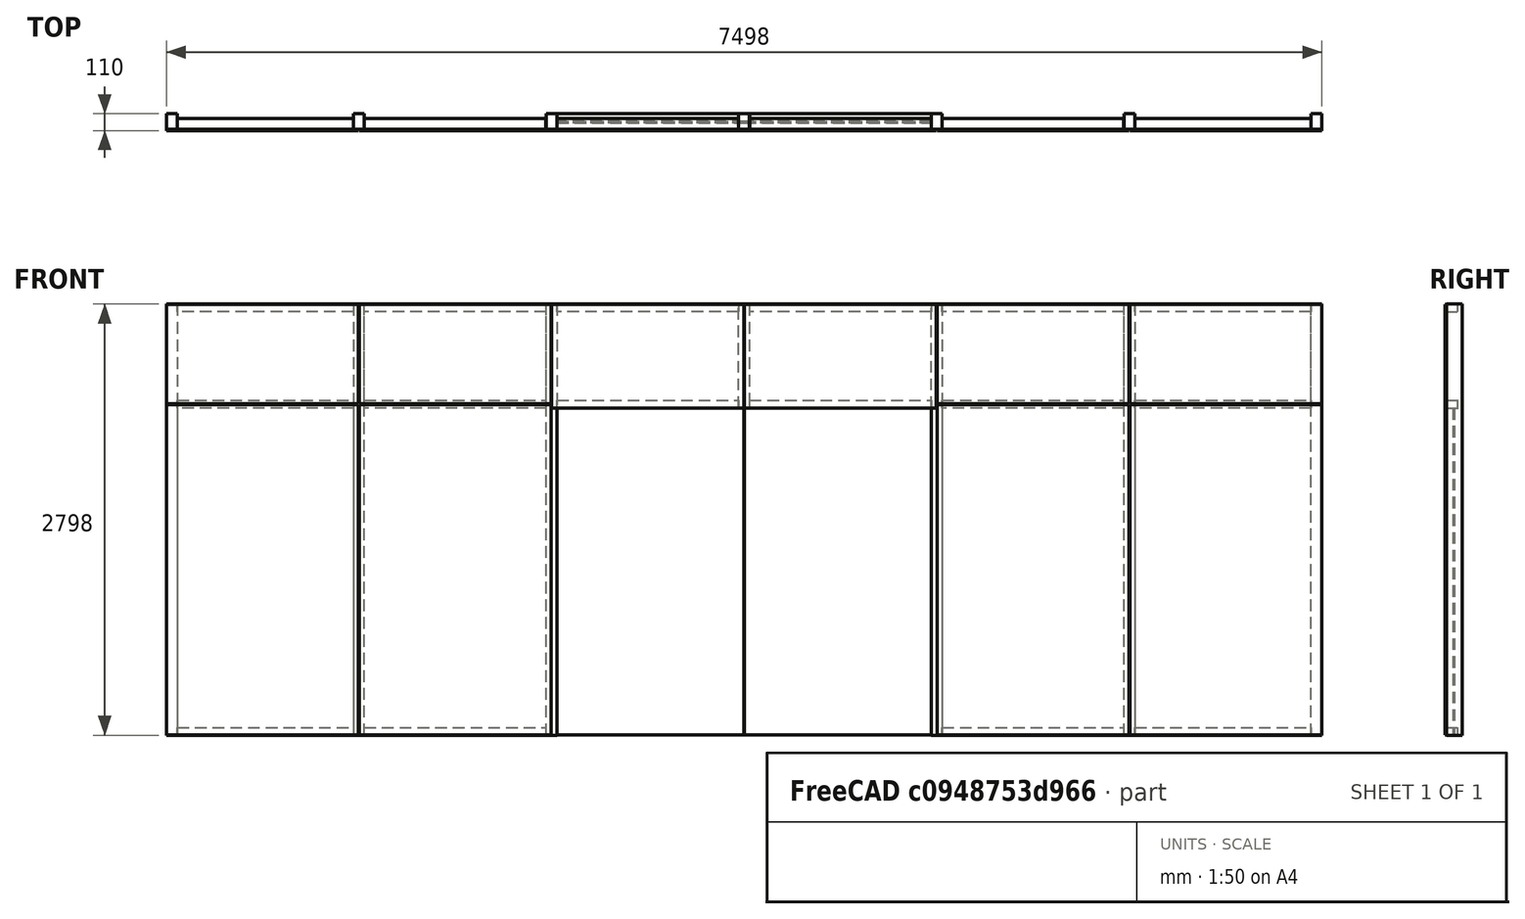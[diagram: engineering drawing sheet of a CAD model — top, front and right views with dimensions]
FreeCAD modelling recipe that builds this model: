
FCSTD DOCUMENT  (FreeCAD 0.16R6704 (Git))
Label: glass skin 6 modules and doors
License: CreativeCommons Attribution
LicenseURL: http://creativecommons.org/licenses/by/4.0/
objects: Sketcher::SketchObject×1, Part::FeaturePython×1
note: 2 computed .brp shape members not serialized (recipe doc carries the construction recipe); baked Part::Feature solids carry a one-line shape summary decoded from their .brp

FEATURE [Sketcher::SketchObject] Sketch207  label="Esboço pele de vidro 002"
  Placement = pos=(0,0,0) rot=(1,0,0;1.5708rad)
  sketch-geometry (176):
    g0: LineSegment StartX=0 StartY=0 StartZ=0 EndX=7500 EndY=0 EndZ=0
    g1: LineSegment StartX=7500 StartY=0 StartZ=0 EndX=7500 EndY=2800 EndZ=0
    g2: LineSegment StartX=7500 StartY=2800 StartZ=0 EndX=0 EndY=2800 EndZ=0
    g3: LineSegment StartX=0 StartY=2800 StartZ=0 EndX=0 EndY=0 EndZ=0
    g4: LineSegment StartX=1 StartY=2799 StartZ=0 EndX=71 EndY=2799 EndZ=0
    g5: LineSegment StartX=71 StartY=2799 StartZ=0 EndX=71 EndY=1 EndZ=0
    g6: LineSegment StartX=71 StartY=1 StartZ=0 EndX=1 EndY=1 EndZ=0
    g7: LineSegment StartX=1 StartY=1 StartZ=0 EndX=1 EndY=2799 EndZ=0
    g8: LineSegment StartX=1285 StartY=2799 StartZ=0 EndX=1215 EndY=2799 EndZ=0
    g9: LineSegment StartX=1215 StartY=2799 StartZ=0 EndX=1215 EndY=1 EndZ=0
    g10: LineSegment StartX=1215 StartY=1 StartZ=0 EndX=1285 EndY=1 EndZ=0
    g11: LineSegment StartX=1285 StartY=1 StartZ=0 EndX=1285 EndY=2799 EndZ=0
    g12: LineSegment StartX=72 StartY=2799 StartZ=0 EndX=1214 EndY=2799 EndZ=0
    g13: LineSegment StartX=1214 StartY=2799 StartZ=0 EndX=1214 EndY=2749 EndZ=0
    g14: LineSegment StartX=1214 StartY=2749 StartZ=0 EndX=72 EndY=2749 EndZ=0
    g15: LineSegment StartX=72 StartY=2749 StartZ=0 EndX=72 EndY=2799 EndZ=0
    g16: LineSegment StartX=72 StartY=2175 StartZ=0 EndX=1214 EndY=2175 EndZ=0
    g17: LineSegment StartX=1214 StartY=2175 StartZ=0 EndX=1214 EndY=2125 EndZ=0
    g18: LineSegment StartX=1214 StartY=2125 StartZ=0 EndX=72 EndY=2125 EndZ=0
    g19: LineSegment StartX=72 StartY=2125 StartZ=0 EndX=72 EndY=2175 EndZ=0
    g20: LineSegment StartX=72 StartY=51 StartZ=0 EndX=1214 EndY=51 EndZ=0
    g21: LineSegment StartX=1214 StartY=51 StartZ=0 EndX=1214 EndY=1 EndZ=0
    g22: LineSegment StartX=1214 StartY=1 StartZ=0 EndX=72 EndY=1 EndZ=0
    g23: LineSegment StartX=72 StartY=1 StartZ=0 EndX=72 EndY=51 EndZ=0
    g24: LineSegment [constr] StartX=0 StartY=4045.56 StartZ=0 EndX=0 EndY=0 EndZ=0
    g25: LineSegment [constr] StartX=1250 StartY=4032 StartZ=0 EndX=1250 EndY=-1064.23 EndZ=0
    g26: LineSegment [constr] StartX=2500 StartY=4059.26 StartZ=0 EndX=2500 EndY=-1119 EndZ=0
    g27: LineSegment [constr] StartX=3750 StartY=3908.57 StartZ=0 EndX=3750 EndY=-1023 EndZ=0
    g28: LineSegment [constr] StartX=5000 StartY=3990.77 StartZ=0 EndX=5000 EndY=-934.694 EndZ=0
    g29: LineSegment [constr] StartX=6250 StartY=4286.35 StartZ=0 EndX=6250 EndY=-1160 EndZ=0
    g30: LineSegment [constr] StartX=7500 StartY=4004.47 StartZ=0 EndX=7500 EndY=0 EndZ=0
    g31: LineSegment [constr] StartX=-2084.05 StartY=2150 StartZ=0 EndX=-4913.6 EndY=2150 EndZ=0
    g32: LineSegment [constr] StartX=0 StartY=3388 StartZ=0 EndX=1250 EndY=3388 EndZ=0
    g33: LineSegment [constr] StartX=1250 StartY=3579.79 StartZ=0 EndX=2500 EndY=3579.79 EndZ=0
    g34: LineSegment [constr] StartX=2500 StartY=3223.61 StartZ=0 EndX=3750 EndY=3223.61 EndZ=0
    g35: LineSegment [constr] StartX=3750 StartY=3538.69 StartZ=0 EndX=5000 EndY=3538.69 EndZ=0
    g36: LineSegment [constr] StartX=5000 StartY=3210 StartZ=0 EndX=6250 EndY=3210 EndZ=0
    g37: LineSegment [constr] StartX=6250 StartY=3579.79 StartZ=0 EndX=7500 EndY=3579.79 EndZ=0
    g38: LineSegment [constr] StartX=287.264 StartY=2799 StartZ=0 EndX=287.264 EndY=2749 EndZ=0
    g39: LineSegment [constr] StartX=206.222 StartY=2175 StartZ=0 EndX=206.222 EndY=2125 EndZ=0
    g40: LineSegment [constr] StartX=1 StartY=2367.03 StartZ=0 EndX=71 EndY=2367.03 EndZ=0
    g41: LineSegment [constr] StartX=1215 StartY=2396.22 StartZ=0 EndX=1285 EndY=2396.22 EndZ=0
    g42: LineSegment [constr] StartX=456.696 StartY=51 StartZ=0 EndX=456.696 EndY=1 EndZ=0
    g43: LineSegment StartX=2.5 StartY=2797.5 StartZ=0 EndX=1247.5 EndY=2797.5 EndZ=0
    g44: LineSegment StartX=1247.5 StartY=2797.5 StartZ=0 EndX=1247.5 EndY=2152.5 EndZ=0
    g45: LineSegment StartX=1247.5 StartY=2152.5 StartZ=0 EndX=2.5 EndY=2152.5 EndZ=0
    g46: LineSegment StartX=2.5 StartY=2152.5 StartZ=0 EndX=2.5 EndY=2797.5 EndZ=0
    g47: LineSegment StartX=2465 StartY=2799 StartZ=0 EndX=2535 EndY=2799 EndZ=0
    g48: LineSegment StartX=2535 StartY=2799 StartZ=0 EndX=2535 EndY=1 EndZ=0
    g49: LineSegment StartX=2535 StartY=1 StartZ=0 EndX=2465 EndY=1 EndZ=0
    g50: LineSegment StartX=2465 StartY=1 StartZ=0 EndX=2465 EndY=2799 EndZ=0
    g51: LineSegment StartX=3715 StartY=2799 StartZ=0 EndX=3785 EndY=2799 EndZ=0
    g52: LineSegment StartX=3785 StartY=2799 StartZ=0 EndX=3785 EndY=2125 EndZ=0
    g53: LineSegment StartX=3785 StartY=2125 StartZ=0 EndX=3715 EndY=2125 EndZ=0
    g54: LineSegment StartX=3715 StartY=2125 StartZ=0 EndX=3715 EndY=2799 EndZ=0
    g55: LineSegment StartX=4965 StartY=2799 StartZ=0 EndX=5035 EndY=2799 EndZ=0
    g56: LineSegment StartX=5035 StartY=2799 StartZ=0 EndX=5035 EndY=1 EndZ=0
    g57: LineSegment StartX=5035 StartY=1 StartZ=0 EndX=4965 EndY=1 EndZ=0
    g58: LineSegment StartX=4965 StartY=1 StartZ=0 EndX=4965 EndY=2799 EndZ=0
    g59: LineSegment StartX=6215 StartY=2799 StartZ=0 EndX=6285 EndY=2799 EndZ=0
    g60: LineSegment StartX=6285 StartY=2799 StartZ=0 EndX=6285 EndY=1 EndZ=0
    g61: LineSegment StartX=6285 StartY=1 StartZ=0 EndX=6215 EndY=1 EndZ=0
    g62: LineSegment StartX=6215 StartY=1 StartZ=0 EndX=6215 EndY=2799 EndZ=0
    g63: LineSegment StartX=7429 StartY=2799 StartZ=0 EndX=7499 EndY=2799 EndZ=0
    g64: LineSegment StartX=7499 StartY=2799 StartZ=0 EndX=7499 EndY=1 EndZ=0
    g65: LineSegment StartX=7499 StartY=1 StartZ=0 EndX=7429 EndY=1 EndZ=0
    g66: LineSegment StartX=7429 StartY=1 StartZ=0 EndX=7429 EndY=2799 EndZ=0
    g67: LineSegment [constr] StartX=2465 StartY=1674.46 StartZ=0 EndX=2535 EndY=1674.46 EndZ=0
    g68: LineSegment [constr] StartX=3715 StartY=1674.45 StartZ=0 EndX=3785 EndY=1674.45 EndZ=0
    g69: LineSegment [constr] StartX=4965 StartY=1669.74 StartZ=0 EndX=5035 EndY=1669.74 EndZ=0
    g70: LineSegment [constr] StartX=6215 StartY=1602 StartZ=0 EndX=6285 EndY=1602 EndZ=0
    g71: LineSegment [constr] StartX=7429 StartY=1550.78 StartZ=0 EndX=7499 EndY=1550.78 EndZ=0
    g72: LineSegment StartX=1286 StartY=2799 StartZ=0 EndX=2464 EndY=2799 EndZ=0
    g73: LineSegment StartX=2464 StartY=2799 StartZ=0 EndX=2464 EndY=2749 EndZ=0
    g74: LineSegment StartX=2464 StartY=2749 StartZ=0 EndX=1286 EndY=2749 EndZ=0
    g75: LineSegment StartX=1286 StartY=2749 StartZ=0 EndX=1286 EndY=2799 EndZ=0
    g76: LineSegment StartX=1286 StartY=2175 StartZ=0 EndX=2464 EndY=2175 EndZ=0
    g77: LineSegment StartX=2464 StartY=2175 StartZ=0 EndX=2464 EndY=2125 EndZ=0
    g78: LineSegment StartX=2464 StartY=2125 StartZ=0 EndX=1286 EndY=2125 EndZ=0
    g79: LineSegment StartX=1286 StartY=2125 StartZ=0 EndX=1286 EndY=2175 EndZ=0
    g80: LineSegment StartX=1286 StartY=51 StartZ=0 EndX=2464 EndY=51 EndZ=0
    g81: LineSegment StartX=2464 StartY=51 StartZ=0 EndX=2464 EndY=1 EndZ=0
    g82: LineSegment StartX=2464 StartY=1 StartZ=0 EndX=1286 EndY=1 EndZ=0
    g83: LineSegment StartX=1286 StartY=1 StartZ=0 EndX=1286 EndY=51 EndZ=0
    g84: LineSegment StartX=1252.5 StartY=2797.5 StartZ=0 EndX=2497.5 EndY=2797.5 EndZ=0
    g85: LineSegment StartX=2497.5 StartY=2797.5 StartZ=0 EndX=2497.5 EndY=2152.5 EndZ=0
    g86: LineSegment StartX=2497.5 StartY=2152.5 StartZ=0 EndX=1252.5 EndY=2152.5 EndZ=0
    g87: LineSegment StartX=1252.5 StartY=2152.5 StartZ=0 EndX=1252.5 EndY=2797.5 EndZ=0
    g88: LineSegment StartX=2536 StartY=2799 StartZ=0 EndX=3714 EndY=2799 EndZ=0
    g89: LineSegment StartX=3714 StartY=2799 StartZ=0 EndX=3714 EndY=2749 EndZ=0
    g90: LineSegment StartX=3714 StartY=2749 StartZ=0 EndX=2536 EndY=2749 EndZ=0
    g91: LineSegment StartX=2536 StartY=2749 StartZ=0 EndX=2536 EndY=2799 EndZ=0
    g92: LineSegment StartX=2536 StartY=2175 StartZ=0 EndX=3714 EndY=2175 EndZ=0
    g93: LineSegment StartX=3714 StartY=2175 StartZ=0 EndX=3714 EndY=2125 EndZ=0
    g94: LineSegment StartX=3714 StartY=2125 StartZ=0 EndX=2536 EndY=2125 EndZ=0
    g95: LineSegment StartX=2536 StartY=2125 StartZ=0 EndX=2536 EndY=2175 EndZ=0
    g96: LineSegment StartX=2536 StartY=51 StartZ=0 EndX=3714 EndY=51 EndZ=0
    g97: LineSegment StartX=3714 StartY=51 StartZ=0 EndX=3714 EndY=1 EndZ=0
    g98: LineSegment StartX=3714 StartY=1 StartZ=0 EndX=2536 EndY=1 EndZ=0
    g99: LineSegment StartX=2536 StartY=1 StartZ=0 EndX=2536 EndY=51 EndZ=0
    g100: LineSegment StartX=3786 StartY=2799 StartZ=0 EndX=4964 EndY=2799 EndZ=0
    g101: LineSegment StartX=4964 StartY=2799 StartZ=0 EndX=4964 EndY=2749 EndZ=0
    g102: LineSegment StartX=4964 StartY=2749 StartZ=0 EndX=3786 EndY=2749 EndZ=0
    g103: LineSegment StartX=3786 StartY=2749 StartZ=0 EndX=3786 EndY=2799 EndZ=0
    g104: LineSegment StartX=3786 StartY=2175 StartZ=0 EndX=4964 EndY=2175 EndZ=0
    g105: LineSegment StartX=4964 StartY=2175 StartZ=0 EndX=4964 EndY=2125 EndZ=0
    g106: LineSegment StartX=4964 StartY=2125 StartZ=0 EndX=3786 EndY=2125 EndZ=0
    g107: LineSegment StartX=3786 StartY=2125 StartZ=0 EndX=3786 EndY=2175 EndZ=0
    g108: LineSegment StartX=3786 StartY=51 StartZ=0 EndX=4964 EndY=51 EndZ=0
    g109: LineSegment StartX=4964 StartY=51 StartZ=0 EndX=4964 EndY=1 EndZ=0
    g110: LineSegment StartX=4964 StartY=1 StartZ=0 EndX=3786 EndY=1 EndZ=0
    g111: LineSegment StartX=3786 StartY=1 StartZ=0 EndX=3786 EndY=51 EndZ=0
    g112: LineSegment StartX=5036 StartY=2799 StartZ=0 EndX=6214 EndY=2799 EndZ=0
    g113: LineSegment StartX=6214 StartY=2799 StartZ=0 EndX=6214 EndY=2749 EndZ=0
    g114: LineSegment StartX=6214 StartY=2749 StartZ=0 EndX=5036 EndY=2749 EndZ=0
    g115: LineSegment StartX=5036 StartY=2749 StartZ=0 EndX=5036 EndY=2799 EndZ=0
    g116: LineSegment StartX=5036 StartY=2175 StartZ=0 EndX=6214 EndY=2175 EndZ=0
    g117: LineSegment StartX=6214 StartY=2175 StartZ=0 EndX=6214 EndY=2125 EndZ=0
    g118: LineSegment StartX=6214 StartY=2125 StartZ=0 EndX=5036 EndY=2125 EndZ=0
    g119: LineSegment StartX=5036 StartY=2125 StartZ=0 EndX=5036 EndY=2175 EndZ=0
    g120: LineSegment StartX=5036 StartY=51 StartZ=0 EndX=6214 EndY=51 EndZ=0
    g121: LineSegment StartX=6214 StartY=51 StartZ=0 EndX=6214 EndY=1 EndZ=0
    g122: LineSegment StartX=6214 StartY=1 StartZ=0 EndX=5036 EndY=1 EndZ=0
    g123: LineSegment StartX=5036 StartY=1 StartZ=0 EndX=5036 EndY=51 EndZ=0
    g124: LineSegment StartX=6286 StartY=2799 StartZ=0 EndX=7428 EndY=2799 EndZ=0
    g125: LineSegment StartX=7428 StartY=2799 StartZ=0 EndX=7428 EndY=2749 EndZ=0
    g126: LineSegment StartX=7428 StartY=2749 StartZ=0 EndX=6286 EndY=2749 EndZ=0
    g127: LineSegment StartX=6286 StartY=2749 StartZ=0 EndX=6286 EndY=2799 EndZ=0
    g128: LineSegment StartX=6286 StartY=2175 StartZ=0 EndX=7428 EndY=2175 EndZ=0
    g129: LineSegment StartX=7428 StartY=2175 StartZ=0 EndX=7428 EndY=2125 EndZ=0
    g130: LineSegment StartX=7428 StartY=2125 StartZ=0 EndX=6286 EndY=2125 EndZ=0
    g131: LineSegment StartX=6286 StartY=2125 StartZ=0 EndX=6286 EndY=2175 EndZ=0
    g132: LineSegment StartX=6286 StartY=51 StartZ=0 EndX=7428 EndY=51 EndZ=0
    g133: LineSegment StartX=7428 StartY=51 StartZ=0 EndX=7428 EndY=1 EndZ=0
    g134: LineSegment StartX=7428 StartY=1 StartZ=0 EndX=6286 EndY=1 EndZ=0
    g135: LineSegment StartX=6286 StartY=1 StartZ=0 EndX=6286 EndY=51 EndZ=0
    g136: LineSegment StartX=2502.5 StartY=2797.5 StartZ=0 EndX=3747.5 EndY=2797.5 EndZ=0
    g137: LineSegment StartX=3747.5 StartY=2797.5 StartZ=0 EndX=3747.5 EndY=2125 EndZ=0
    g138: LineSegment StartX=3747.5 StartY=2125 StartZ=0 EndX=2502.5 EndY=2125 EndZ=0
    g139: LineSegment StartX=2502.5 StartY=2125 StartZ=0 EndX=2502.5 EndY=2797.5 EndZ=0
    g140: LineSegment StartX=3752.5 StartY=2125 StartZ=0 EndX=4997.5 EndY=2125 EndZ=0
    g141: LineSegment StartX=4997.5 StartY=2125 StartZ=0 EndX=4997.5 EndY=2797.5 EndZ=0
    g142: LineSegment StartX=4997.5 StartY=2797.5 StartZ=0 EndX=3752.5 EndY=2797.5 EndZ=0
    g143: LineSegment StartX=3752.5 StartY=2797.5 StartZ=0 EndX=3752.5 EndY=2125 EndZ=0
    g144: LineSegment StartX=5002.5 StartY=2797.5 StartZ=0 EndX=6247.5 EndY=2797.5 EndZ=0
    g145: LineSegment StartX=6247.5 StartY=2797.5 StartZ=0 EndX=6247.5 EndY=2152.5 EndZ=0
    g146: LineSegment StartX=6247.5 StartY=2152.5 StartZ=0 EndX=5002.5 EndY=2152.5 EndZ=0
    g147: LineSegment StartX=5002.5 StartY=2152.5 StartZ=0 EndX=5002.5 EndY=2797.5 EndZ=0
    g148: LineSegment StartX=6252.5 StartY=2152.5 StartZ=0 EndX=7497.5 EndY=2152.5 EndZ=0
    g149: LineSegment StartX=7497.5 StartY=2152.5 StartZ=0 EndX=7497.5 EndY=2797.5 EndZ=0
    g150: LineSegment StartX=7497.5 StartY=2797.5 StartZ=0 EndX=6252.5 EndY=2797.5 EndZ=0
    g151: LineSegment StartX=6252.5 StartY=2797.5 StartZ=0 EndX=6252.5 EndY=2152.5 EndZ=0
    g152: LineSegment StartX=2536 StartY=2124 StartZ=0 EndX=3747.5 EndY=2124 EndZ=0
    g153: LineSegment StartX=3747.5 StartY=2124 StartZ=0 EndX=3747.5 EndY=2.5 EndZ=0
    g154: LineSegment StartX=3747.5 StartY=2.5 StartZ=0 EndX=2536 EndY=2.5 EndZ=0
    g155: LineSegment StartX=2536 StartY=2.5 StartZ=0 EndX=2536 EndY=2124 EndZ=0
    g156: LineSegment StartX=3752.5 StartY=2.5 StartZ=0 EndX=4964 EndY=2.5 EndZ=0
    g157: LineSegment StartX=4964 StartY=2.5 StartZ=0 EndX=4964 EndY=2124 EndZ=0
    g158: LineSegment StartX=4964 StartY=2124 StartZ=0 EndX=3752.5 EndY=2124 EndZ=0
    g159: LineSegment StartX=3752.5 StartY=2124 StartZ=0 EndX=3752.5 EndY=2.5 EndZ=0
    g160: LineSegment StartX=2.5 StartY=2147.5 StartZ=0 EndX=1247.5 EndY=2147.5 EndZ=0
    g161: LineSegment StartX=1247.5 StartY=2147.5 StartZ=0 EndX=1247.5 EndY=2.5 EndZ=0
    g162: LineSegment StartX=1247.5 StartY=2.5 StartZ=0 EndX=2.5 EndY=2.5 EndZ=0
    g163: LineSegment StartX=2.5 StartY=2.5 StartZ=0 EndX=2.5 EndY=2147.5 EndZ=0
    g164: LineSegment StartX=1252.5 StartY=2147.5 StartZ=0 EndX=2497.5 EndY=2147.5 EndZ=0
    g165: LineSegment StartX=2497.5 StartY=2147.5 StartZ=0 EndX=2497.5 EndY=2.5 EndZ=0
    g166: LineSegment StartX=2497.5 StartY=2.5 StartZ=0 EndX=1252.5 EndY=2.5 EndZ=0
    g167: LineSegment StartX=1252.5 StartY=2.5 StartZ=0 EndX=1252.5 EndY=2147.5 EndZ=0
    g168: LineSegment StartX=5002.5 StartY=2147.5 StartZ=0 EndX=6247.5 EndY=2147.5 EndZ=0
    g169: LineSegment StartX=6247.5 StartY=2147.5 StartZ=0 EndX=6247.5 EndY=2.5 EndZ=0
    g170: LineSegment StartX=6247.5 StartY=2.5 StartZ=0 EndX=5002.5 EndY=2.5 EndZ=0
    g171: LineSegment StartX=5002.5 StartY=2.5 StartZ=0 EndX=5002.5 EndY=2147.5 EndZ=0
    g172: LineSegment StartX=6252.5 StartY=2147.5 StartZ=0 EndX=7497.5 EndY=2147.5 EndZ=0
    g173: LineSegment StartX=7497.5 StartY=2147.5 StartZ=0 EndX=7497.5 EndY=2.5 EndZ=0
    g174: LineSegment StartX=7497.5 StartY=2.5 StartZ=0 EndX=6252.5 EndY=2.5 EndZ=0
    g175: LineSegment StartX=6252.5 StartY=2.5 StartZ=0 EndX=6252.5 EndY=2147.5 EndZ=0
  constraints (509):
    c: Coincident(g0,g1)
    c: Coincident(g1,g2)
    c: Coincident(g2,g3)
    c: Coincident(g3,g0)
    c: Horizontal(g0)
    c: Horizontal(g2)
    c: Vertical(g1)
    c: Vertical(g3)
    c: Coincident(g0,g-1)
    c: DistanceX(g2,g1) = 7500  'Largura do vão'
    c: DistanceY(g-1,g2) = 2800  'Altura do vão'
    c: Coincident(g4,g5)
    c: Coincident(g5,g6)
    c: Coincident(g6,g7)
    c: Coincident(g7,g4)
    c: Horizontal(g4)
    c: Horizontal(g6)
    c: Vertical(g5)
    c: Vertical(g7)
    c: Coincident(g8,g9)
    c: Coincident(g9,g10)
    c: Coincident(g10,g11)
    c: Coincident(g11,g8)
    c: Horizontal(g8)
    c: Horizontal(g10)
    c: Vertical(g9)
    c: Vertical(g11)
    c: Coincident(g12,g13)
    c: Coincident(g13,g14)
    c: Coincident(g14,g15)
    c: Coincident(g15,g12)
    c: Horizontal(g12)
    c: Horizontal(g14)
    c: Vertical(g13)
    c: Vertical(g15)
    c: Coincident(g16,g17)
    c: Coincident(g17,g18)
    c: Coincident(g18,g19)
    c: Coincident(g19,g16)
    c: Horizontal(g16)
    c: Horizontal(g18)
    c: Vertical(g17)
    c: Vertical(g19)
    c: Coincident(g20,g21)
    c: Coincident(g21,g22)
    c: Coincident(g22,g23)
    c: Coincident(g23,g20)
    c: Horizontal(g20)
    c: Horizontal(g22)
    c: Vertical(g21)
    c: Vertical(g23)
    c: Vertical(g24)
    c: Vertical(g30)
    c: PointOnObject(g32,g24)
    c: PointOnObject(g32,g25)
    c: PointOnObject(g33,g25)
    c: PointOnObject(g33,g26)
    c: PointOnObject(g34,g26)
    c: PointOnObject(g34,g27)
    c: PointOnObject(g35,g27)
    c: PointOnObject(g35,g28)
    c: PointOnObject(g36,g28)
    c: PointOnObject(g36,g29)
    c: PointOnObject(g37,g29)
    c: PointOnObject(g37,g30)
    c: Equal(g32,g33)
    c: Equal(g33,g34)
    c: Equal(g34,g35)
    c: Equal(g35,g36)
    c: Equal(g36,g37)
    c: Angle(g32) = 0
    c: Angle(g33) = 0
    c: Angle(g34) = 0
    c: Angle(g35) = 0
    c: Angle(g36) = 0
    c: Angle(g37) = 0
    c: Coincident(g24,g-1)
    c: Coincident(g30,g0)
    c: DistanceY(g-1,g31) = 2150  'Altura da divisão horizontal (eixo)'
    c: Symmetric(g16,g18,g31)  'Constraint85'
    c: Symmetric(g8,g8,g25)  'Constraint84'
    c: DistanceY(g12,g2) = 1  'Constraint83'
    c: DistanceY(g14,g12) = 50  'Altura dos perfis horizontais'
    c: DistanceX(g16,g14) = 0  'Constraint88'
    c: PointOnObject(g38,g12)  'Constraint87'
    c: PointOnObject(g38,g14)  'Constraint86'
    c: PointOnObject(g39,g16)
    c: PointOnObject(g39,g18)
    c: Angle(g38) = -1.5708
    c: Angle(g39) = -1.5708
    c: DistanceX(g2,g4) = 1
    c: DistanceY(g4,g2) = 1
    c: DistanceY(g-1,g6) = 1
    c: DistanceX(g4,g4) = 70  'Largura perfis verticais'
    c: PointOnObject(g40,g7)  'Constraint101'
    c: PointOnObject(g40,g5)
    c: Angle(g40) = 0
    c: DistanceX(g4,g12) = 1
    c: PointOnObject(g41,g9)
    c: PointOnObject(g41,g11)
    c: Angle(g41) = 0
    c: DistanceY(g8,g4) = 0
    c: DistanceY(g5,g9) = 0
    c: PointOnObject(g42,g20)
    c: PointOnObject(g42,g22)
    c: Angle(g42) = -1.5708
    c: DistanceX(g20,g18) = 0
    c: DistanceY(g5,g22) = 0
    c: Equal(g38,g39)
    c: Equal(g39,g42)
    c: DistanceX(g12,g8) = 1
    c: DistanceX(g13,g16) = 0
    c: DistanceX(g17,g20) = 0
    c: Coincident(g43,g44)
    c: Coincident(g44,g45)
    c: Coincident(g45,g46)
    c: Coincident(g46,g43)
    c: Horizontal(g43)
    c: Horizontal(g45)
    c: Vertical(g44)
    c: Vertical(g46)
    c: DistanceY(g43,g4) = 1.5
    c: DistanceX(g4,g43) = 1.5
    c: Coincident(g47,g48)
    c: Coincident(g48,g49)
    c: Coincident(g49,g50)
    c: Coincident(g50,g47)
    c: Horizontal(g47)
    c: Horizontal(g49)
    c: Vertical(g48)
    c: Vertical(g50)
    c: Coincident(g51,g52)
    c: Coincident(g52,g53)
    c: Coincident(g53,g54)
    c: Coincident(g54,g51)
    c: Horizontal(g51)
    c: Horizontal(g53)
    c: Vertical(g52)
    c: Vertical(g54)
    c: Coincident(g55,g56)
    c: Coincident(g56,g57)
    c: Coincident(g57,g58)
    c: Coincident(g58,g55)
    c: Horizontal(g55)
    c: Horizontal(g57)
    c: Vertical(g56)
    c: Vertical(g58)
    c: Coincident(g59,g60)
    c: Coincident(g60,g61)
    c: Coincident(g61,g62)
    c: Coincident(g62,g59)
    c: Horizontal(g59)
    c: Horizontal(g61)
    c: Vertical(g60)
    c: Vertical(g62)
    c: Coincident(g63,g64)
    c: Coincident(g64,g65)
    c: Coincident(g65,g66)
    c: Coincident(g66,g63)
    c: Horizontal(g63)
    c: Horizontal(g65)
    c: Vertical(g64)
    c: Vertical(g66)
    c: DistanceY(g47,g8) = 0
    c: Symmetric(g47,g47,g26)
    c: DistanceY(g51,g47) = 0
    c: Symmetric(g51,g51,g27)
    c: DistanceY(g55,g51) = 0
    c: Symmetric(g55,g55,g28)
    c: DistanceY(g55,g59) = 0
    c: Symmetric(g59,g59,g29)
    c: DistanceY(g63,g59) = 0
    c: DistanceX(g63,g1) = 1
    c: DistanceY(g10,g49) = 0
    c: DistanceY(g56,g61) = 0
    c: DistanceY(g60,g65) = 0
    c: PointOnObject(g67,g50)
    c: PointOnObject(g67,g48)
    c: PointOnObject(g68,g54)
    c: PointOnObject(g68,g52)
    c: PointOnObject(g69,g58)
    c: PointOnObject(g69,g56)
    c: PointOnObject(g70,g62)
    c: PointOnObject(g70,g60)
    c: PointOnObject(g71,g66)
    c: PointOnObject(g71,g64)
    c: Angle(g71) = 0
    c: Angle(g70) = 0
    c: Angle(g69) = 0
    c: Angle(g68) = 0
    c: Angle(g67) = 0
    c: Equal(g40,g41)
    c: Equal(g41,g67)
    c: Equal(g67,g68)
    c: Equal(g68,g69)
    c: Equal(g69,g70)
    c: Equal(g70,g71)
    c: Coincident(g72,g73)
    c: Coincident(g73,g74)
    c: Coincident(g74,g75)
    c: Coincident(g75,g72)
    c: Horizontal(g72)
    c: Horizontal(g74)
    c: Vertical(g73)
    c: Vertical(g75)
    c: Coincident(g76,g77)
    c: Coincident(g77,g78)
    c: Coincident(g78,g79)
    c: Coincident(g79,g76)
    c: Horizontal(g76)
    c: Horizontal(g78)
    c: Vertical(g77)
    c: Vertical(g79)
    c: Coincident(g80,g81)
    c: Coincident(g81,g82)
    c: Coincident(g82,g83)
    c: Coincident(g83,g80)
    c: Horizontal(g80)
    c: Horizontal(g82)
    c: Vertical(g81)
    c: Vertical(g83)
    c: DistanceX(g8,g72) = 1
    c: DistanceY(g72,g12) = 0
    c: DistanceY(g74,g13) = 0
    c: DistanceX(g74,g76) = 0
    c: DistanceY(g16,g76) = 0
    c: DistanceY(g78,g17) = 0
    c: DistanceX(g78,g80) = 0
    c: DistanceY(g21,g82) = 0
    c: DistanceY(g20,g80) = 0
    c: DistanceX(g72,g47) = 1
    c: DistanceX(g76,g73) = 0
    c: DistanceX(g80,g77) = 0
    c: Coincident(g84,g85)
    c: Coincident(g85,g86)
    c: Coincident(g86,g87)
    c: Coincident(g87,g84)
    c: Horizontal(g84)
    c: Horizontal(g86)
    c: Vertical(g85)
    c: Vertical(g87)
    c: DistanceY(g84,g43) = 0
    c: DistanceY(g44,g86) = 0
    c: Symmetric(g44,g86,g25)
    c: DistanceX(g44,g86) = 5
    c: Coincident(g88,g89)
    c: Coincident(g89,g90)
    c: Coincident(g90,g91)
    c: Coincident(g91,g88)
    c: Horizontal(g88)
    c: Horizontal(g90)
    c: Vertical(g89)
    c: Vertical(g91)
    c: Coincident(g92,g93)
    c: Coincident(g93,g94)
    c: Coincident(g95,g92)
    c: Horizontal(g92)
    c: Horizontal(g94)
    c: Vertical(g93)
    c: Vertical(g95)
    c: Coincident(g96,g97)
    c: Coincident(g97,g98)
    c: Coincident(g98,g99)
    c: Coincident(g99,g96)
    c: Horizontal(g96)
    c: Horizontal(g98)
    c: Vertical(g97)
    c: Vertical(g99)
    c: Coincident(g100,g101)
    c: Coincident(g101,g102)
    c: Coincident(g102,g103)
    c: Coincident(g103,g100)
    c: Horizontal(g100)
    c: Horizontal(g102)
    c: Vertical(g101)
    c: Vertical(g103)
    c: Coincident(g104,g105)
    c: Coincident(g105,g106)
    c: Coincident(g106,g107)
    c: Coincident(g107,g104)
    c: Horizontal(g104)
    c: Horizontal(g106)
    c: Vertical(g105)
    c: Vertical(g107)
    c: Coincident(g108,g109)
    c: Coincident(g109,g110)
    c: Coincident(g110,g111)
    c: Coincident(g111,g108)
    c: Horizontal(g108)
    c: Horizontal(g110)
    c: Vertical(g109)
    c: Vertical(g111)
    c: Coincident(g112,g113)
    c: Coincident(g113,g114)
    c: Coincident(g114,g115)
    c: Coincident(g115,g112)
    c: Horizontal(g112)
    c: Horizontal(g114)
    c: Vertical(g113)
    c: Vertical(g115)
    c: Coincident(g116,g117)
    c: Coincident(g117,g118)
    c: Coincident(g118,g119)
    c: Coincident(g119,g116)
    c: Horizontal(g116)
    c: Horizontal(g118)
    c: Vertical(g117)
    c: Vertical(g119)
    c: Coincident(g120,g121)
    c: Coincident(g121,g122)
    c: Coincident(g122,g123)
    c: Coincident(g123,g120)
    c: Horizontal(g120)
    c: Horizontal(g122)
    c: Vertical(g121)
    c: Vertical(g123)
    c: Coincident(g124,g125)
    c: Coincident(g125,g126)
    c: Coincident(g126,g127)
    c: Coincident(g127,g124)
    c: Horizontal(g124)
    c: Horizontal(g126)
    c: Vertical(g125)
    c: Vertical(g127)
    c: Coincident(g128,g129)
    c: Coincident(g129,g130)
    c: Coincident(g130,g131)
    c: Coincident(g131,g128)
    c: Horizontal(g128)
    c: Horizontal(g130)
    c: Vertical(g129)
    c: Vertical(g131)
    c: Coincident(g132,g133)
    c: Coincident(g133,g134)
    c: Coincident(g134,g135)
    c: Coincident(g135,g132)
    c: Horizontal(g132)
    c: Horizontal(g134)
    c: Vertical(g133)
    c: Vertical(g135)
    c: DistanceX(g47,g88) = 1
    c: DistanceY(g88,g72) = 0
    c: DistanceY(g90,g73) = 0
    c: DistanceX(g90,g92) = 0
    c: DistanceY(g76,g92) = 0
    c: DistanceY(g94,g77) = 0
    c: DistanceX(g94,g96) = 0
    c: DistanceY(g80,g96) = 0
    c: DistanceY(g81,g98) = 0
    c: DistanceX(g88,g51) = 1
    c: DistanceX(g92,g89) = 0
    c: DistanceX(g96,g93) = 0
    c: DistanceX(g51,g100) = 1
    c: DistanceY(g100,g88) = 0
    c: DistanceY(g102,g89) = 0
    c: DistanceX(g102,g104) = 0
    c: DistanceY(g92,g104) = 0
    c: DistanceY(g106,g93) = 0
    c: DistanceX(g106,g108) = 0
    c: DistanceY(g96,g108) = 0
    c: DistanceX(g100,g55) = 1
    c: DistanceX(g104,g101) = 0
    c: DistanceX(g108,g105) = 0
    c: DistanceX(g55,g112) = 1
    c: DistanceY(g112,g100) = 0
    c: DistanceY(g114,g101) = 0
    c: DistanceX(g114,g116) = 0
    c: DistanceY(g104,g116) = 0
    c: DistanceY(g118,g105) = 0
    c: DistanceX(g118,g120) = 0
    c: DistanceY(g108,g120) = 0
    c: DistanceX(g112,g59) = 1
    c: DistanceX(g116,g113) = 0
    c: DistanceX(g120,g117) = 0
    c: DistanceX(g59,g124) = 1
    c: DistanceY(g124,g112) = 0
    c: DistanceY(g126,g113) = 0
    c: DistanceX(g126,g128) = 0
    c: DistanceY(g116,g128) = 0
    c: DistanceY(g130,g117) = 0
    c: DistanceX(g130,g132) = 0
    c: DistanceY(g120,g132) = 0
    c: DistanceY(g121,g134) = 0
    c: DistanceX(g124,g63) = 1
    c: DistanceX(g128,g125) = 0
    c: DistanceX(g132,g129) = 0
    c: Coincident(g136,g137)
    c: Coincident(g137,g138)
    c: Coincident(g138,g139)
    c: Coincident(g139,g136)
    c: Horizontal(g136)
    c: Horizontal(g138)
    c: Vertical(g137)
    c: Vertical(g139)
    c: Coincident(g140,g141)
    c: Coincident(g141,g142)
    c: Coincident(g142,g143)
    c: Coincident(g143,g140)
    c: Horizontal(g140)
    c: Horizontal(g142)
    c: Vertical(g141)
    c: Vertical(g143)
    c: Coincident(g144,g145)
    c: Coincident(g145,g146)
    c: Coincident(g146,g147)
    c: Coincident(g147,g144)
    c: Horizontal(g144)
    c: Horizontal(g146)
    c: Vertical(g145)
    c: Vertical(g147)
    c: Coincident(g148,g149)
    c: Coincident(g149,g150)
    c: Coincident(g150,g151)
    c: Coincident(g151,g148)
    c: Horizontal(g148)
    c: Horizontal(g150)
    c: Vertical(g149)
    c: Vertical(g151)
    c: DistanceY(g136,g84) = 0
    c: DistanceX(g84,g136) = 5
    c: Symmetric(g84,g136,g26)
    c: DistanceY(g142,g136) = 0
    c: Symmetric(g136,g142,g27)
    c: DistanceX(g136,g142) = 5
    c: DistanceY(g137,g140) = 0
    c: DistanceY(g144,g141) = 0
    c: Symmetric(g141,g144,g28)
    c: DistanceX(g141,g144) = 5
    c: DistanceY(g150,g144) = 0
    c: Symmetric(g144,g150,g29)
    c: DistanceX(g144,g150) = 5
    c: DistanceY(g145,g148) = 0
    c: DistanceX(g149,g63) = 1.5
    c: DistanceY(g77,g138) = 0
    c: Coincident(g152,g153)
    c: Coincident(g153,g154)
    c: Coincident(g154,g155)
    c: Coincident(g155,g152)
    c: Horizontal(g152)
    c: Horizontal(g154)
    c: Vertical(g153)
    c: Vertical(g155)
    c: Coincident(g156,g157)
    c: Coincident(g157,g158)
    c: Coincident(g158,g159)
    c: Coincident(g159,g156)
    c: Horizontal(g156)
    c: Horizontal(g158)
    c: Vertical(g157)
    c: Vertical(g159)
    c: DistanceY(g158,g152) = 0
    c: Symmetric(g152,g158,g27)
    c: DistanceX(g152,g158) = 5
    c: DistanceY(g153,g156) = 0
    c: DistanceY(g53,g93) = 0
    c: DistanceY(g152,g94) = 1
    c: Coincident(g94,g95)
    c: DistanceX(g94,g152) = 0
    c: DistanceX(g105,g157) = 0
    c: DistanceY(g146,g85) = 0
    c: Coincident(g160,g161)
    c: Coincident(g161,g162)
    c: Coincident(g162,g163)
    c: Coincident(g163,g160)
    c: Horizontal(g160)
    c: Horizontal(g162)
    c: Vertical(g161)
    c: Vertical(g163)
    c: Coincident(g164,g165)
    c: Coincident(g165,g166)
    c: Coincident(g166,g167)
    c: Coincident(g167,g164)
    c: Horizontal(g164)
    c: Horizontal(g166)
    c: Vertical(g165)
    c: Vertical(g167)
    c: Coincident(g168,g169)
    c: Coincident(g169,g170)
    c: Coincident(g170,g171)
    c: Coincident(g171,g168)
    c: Horizontal(g168)
    c: Horizontal(g170)
    c: Vertical(g169)
    c: Vertical(g171)
    c: Coincident(g172,g173)
    c: Coincident(g173,g174)
    c: Coincident(g174,g175)
    c: Coincident(g175,g172)
    c: Horizontal(g172)
    c: Horizontal(g174)
    c: Vertical(g173)
    c: Vertical(g175)
    c: DistanceX(g45,g160) = 0
    c: Symmetric(g45,g160,g31)
    c: DistanceY(g160,g45) = 5
    c: DistanceY(g6,g162) = 1.5
    c: DistanceX(g160,g44) = 0
    c: DistanceY(g161,g166) = 0
    c: DistanceX(g86,g164) = 0
    c: DistanceY(g164,g160) = 0
    c: DistanceX(g164,g85) = 0
    c: DistanceY(g168,g164) = 0
    c: DistanceX(g146,g168) = 0
    c: DistanceX(g168,g145) = 0
    c: DistanceY(g165,g170) = 0
    c: DistanceY(g172,g168) = 0
    c: DistanceX(g148,g172) = 0
    c: DistanceX(g172,g148) = 0
    c: DistanceY(g169,g174) = 0
FEATURE [Part::FeaturePython] Window123  label="glass skin 6 modules and doors"  # WARN: FeaturePython — macro-defined, semantics opaque (R4)
  Base = -> Sketch207
  Height = 0
  HoleDepth = 0
  MoveWithHost = true
  Normal = (0,1,0)
  Preset = 0
  Role = 0
  Width = 0
  WindowParts = MONTANTE VERTICAL 1 | Frame | Wire1 | 100.0 | 0.0 | MONTANTE VERTICAL 2 | Frame | Wire2 | 100.0 | 0.0 | MONTANTE VERTICAL 3 | Frame | Wire7 | 100.0 | 0.0 | MONTANTE VERTICAL 4 | Frame | Wire8 | 100 | 0.0 | MONTANTE VERTICAL 5 | Frame | Wire9 | 100.0 | 0.0 | MONTANTE VERTICAL 6 | Frame | Wire10 | 100.0 | 0.0 | MONTANTE VERTICAL 7 | Frame | Wire11 | 100.0 | 0.0 | MONTANTE HORIZONTAL 1 | Frame | Wire3 | 70.0 | 0.0 | MONTANTE HORIZONTAL 2 | Frame | Wire4 | 70.0 | 0.0 | MONTANTE HORIZONTAL 3 | Frame | Wire5 | 70.0 | 0.0 | MONTANTE HORIZONTAL 4 | Frame | Wire12 | 70.0 | 0.0 | MONTANTE HORIZONTAL 5 | Frame | Wire13 | 70.0 | 0.0 | MONTANTE HORIZONTAL 6 | Frame | Wire14 | 70.0 | 0.0 | MONTANTE HORIZONTAL 7 | Frame | Wire16 | 70.0 | 0.0 | MONTANTE HORIZONTAL 8 | Frame | Wire17 | 100.0 | 0.0 | MONTANTE HORIZONTAL 10 | Frame | Wire19 | 70.0 | 0.0 | MONTANTE HORIZONTAL 11 | Frame | Wire20 | 100.0 | 0.0 | MONTANTE HORIZONTAL 13 | Frame | Wire22 | 70.0 | 0.0 | MONTANTE HORIZONTAL 14 | Frame | Wire23 | 70.0 | 0.0 | MONTANTE HORIZONTAL 15 | Frame | Wire24 | 70.0 | 0.0 | MONTANTE HORIZONTAL 16 | Frame | Wire25 | 70.0 | 0.0 | MONTANTE HORIZONTAL 17 | Frame | Wire26 | 70.0 | 0.0 | MONTANTE HORIZONTAL 18 | Frame | Wire27 | 70.0 | 0.0 | VIDRO 1 | Glass panel | Wire6 | 10.0 | -10.0 | VIDRO 2 | Glass panel | Wire15 | 10.0 | -10.0 | VIDRO 3 | Glass panel | Wire28 | 10.0 | -10.0 | VIDRO 4 | Glass panel | Wire29 | 10.0 | -10.0 | VIDRO 5 | Glass panel | Wire30 | 10.0 | -10.0 | VIDRO 6 | Glass panel | Wire31 | 10.0 | -10.0 | PORTA 1 | Glass panel | Wire32 | 10.0 | 40.0 | PORTA 2 | Glass panel | Wire33 | 10.0 | 40.0 | VIDRO 7 | Glass panel | Wire34 | 10.0 | -10.0 | VIDRO 8 | Glass panel | Wire35 | 10.0 | -10.0 | VIDRO 9 | Glass panel | Wire36 | 10.0 | -10.0 | VIDRO 10 | Glass panel | Wire37 | 10.0 | -10.0
